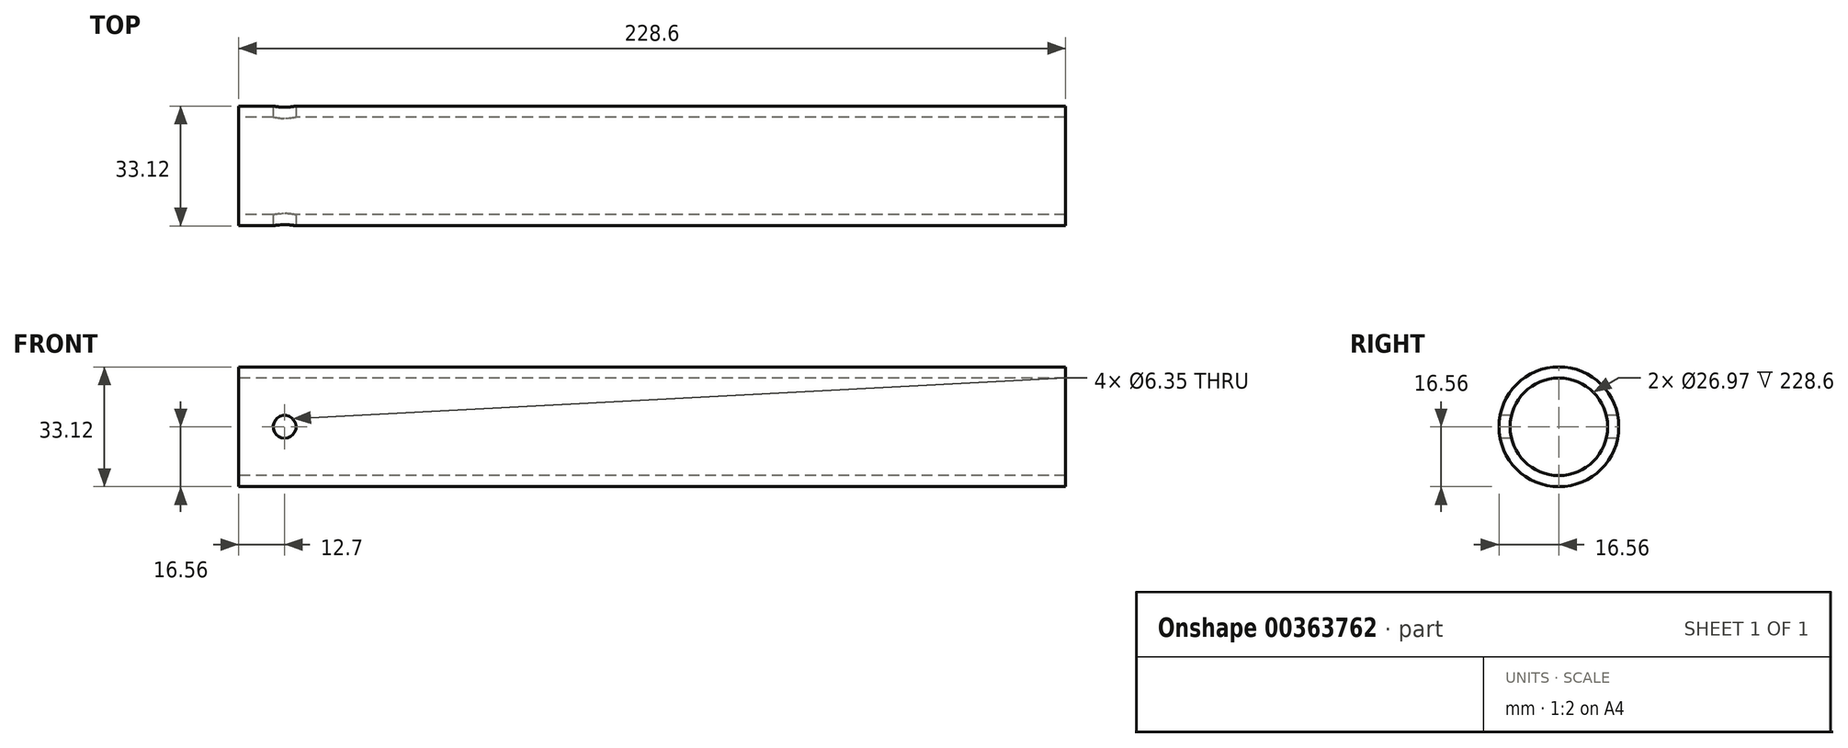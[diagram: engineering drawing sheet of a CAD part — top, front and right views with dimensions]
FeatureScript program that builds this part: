
annotation { "Feature Type Name" : "Feature", "Feature Type Description" : "" }
export const myFeature = defineFeature(function(context is Context, id is Id, definition is map)
    precondition{}
    {
        {
            var Q0;
            Q0=qCreatedBy(makeId("Front.planeOp"),FACE);
            var sketch = newSketch(context, id + "F0", { "sketchPlane" : qUnion([Q0])});
            skLineSegment(sketch, "E0", {"start": v(-108.2, 0) * mm, "end": v(127, 0) * mm, "construction": true});
            skLineSegment(sketch, "E1.bottom", {"start": v(-111.76, 16.56) * mm, "end": v(116.84, 16.56) * mm});
            skLineSegment(sketch, "E1.top", {"start": v(-111.76, 13.49) * mm, "end": v(116.84, 13.49) * mm});
            skLineSegment(sketch, "E1.left", {"start": v(-111.76, 16.56) * mm, "end": v(-111.76, 13.49) * mm});
            skLineSegment(sketch, "E1.right", {"start": v(116.84, 16.56) * mm, "end": v(116.84, 13.49) * mm});
            skLineSegment(sketch, "E2.MirrorCS", {"start": v(-111.76, -16.56) * mm, "end": v(-111.76, -13.49) * mm});
            skLineSegment(sketch, "E3.MirrorCS", {"start": v(116.84, -16.56) * mm, "end": v(116.84, -13.49) * mm});
            skLineSegment(sketch, "E4.MirrorCS", {"start": v(-111.76, -16.56) * mm, "end": v(116.84, -16.56) * mm});
            skLineSegment(sketch, "E5.MirrorCS", {"start": v(-111.76, -13.49) * mm, "end": v(116.84, -13.49) * mm});
            skCircle(sketch, "E6", {"center": v(-99.06, 0) * mm, "radius": 3.18 * mm});
            skLineSegment(sketch, "E7", {"start": v(-99.06, 0) * mm, "end": v(-99.06, 16.56) * mm, "construction": true});
            skSolve(sketch);
        }
        {
            var Q0;
            Q0=makeQuery(id+"F0.imprint","IMPRINT",FACE,{"disambiguationData":[TD([[makeQuery(id+"F0.imprint","IMPRINT",EDGE,{"derivedFrom":sQuery(id+"F0.wireOp",EDGE,"E1.bottom")}),-1.0]])]});
            var Q1;
            Q1=makeQuery(id+"F0.imprint","IMPRINT",FACE,{"disambiguationData":[TD([[makeQuery(id+"F0.imprint","IMPRINT",EDGE,{"derivedFrom":sQuery(id+"F0.wireOp",EDGE,"E3.MirrorCS")}),1.0]])]});
            var Q2;
            Q2=sQuery(id+"F0.wireOp",EDGE,"E0");
            revolve(context, id + "F1", {"entities" : qUnion([Q0, Q1]), "axis" : qUnion([Q2]), "revolveType" : RevolveType.FULL});
        }
        {
            var Q0;
            Q0=makeQuery(id+"F0.imprint","IMPRINT",FACE,{"disambiguationData":[TD([[makeQuery(id+"F0.imprint","IMPRINT",EDGE,{"derivedFrom":sQuery(id+"F0.wireOp",EDGE,"E6")}),1.0]])]});
            extrude(context, id + "F2", {"entities" : qUnion([Q0]), "operationType" : NewBodyOperationType.REMOVE, "endBound" : BoundingType.SYMMETRIC, "oppositeDirection" : true, "depth" : 57.4 * mm});
        }
    });
